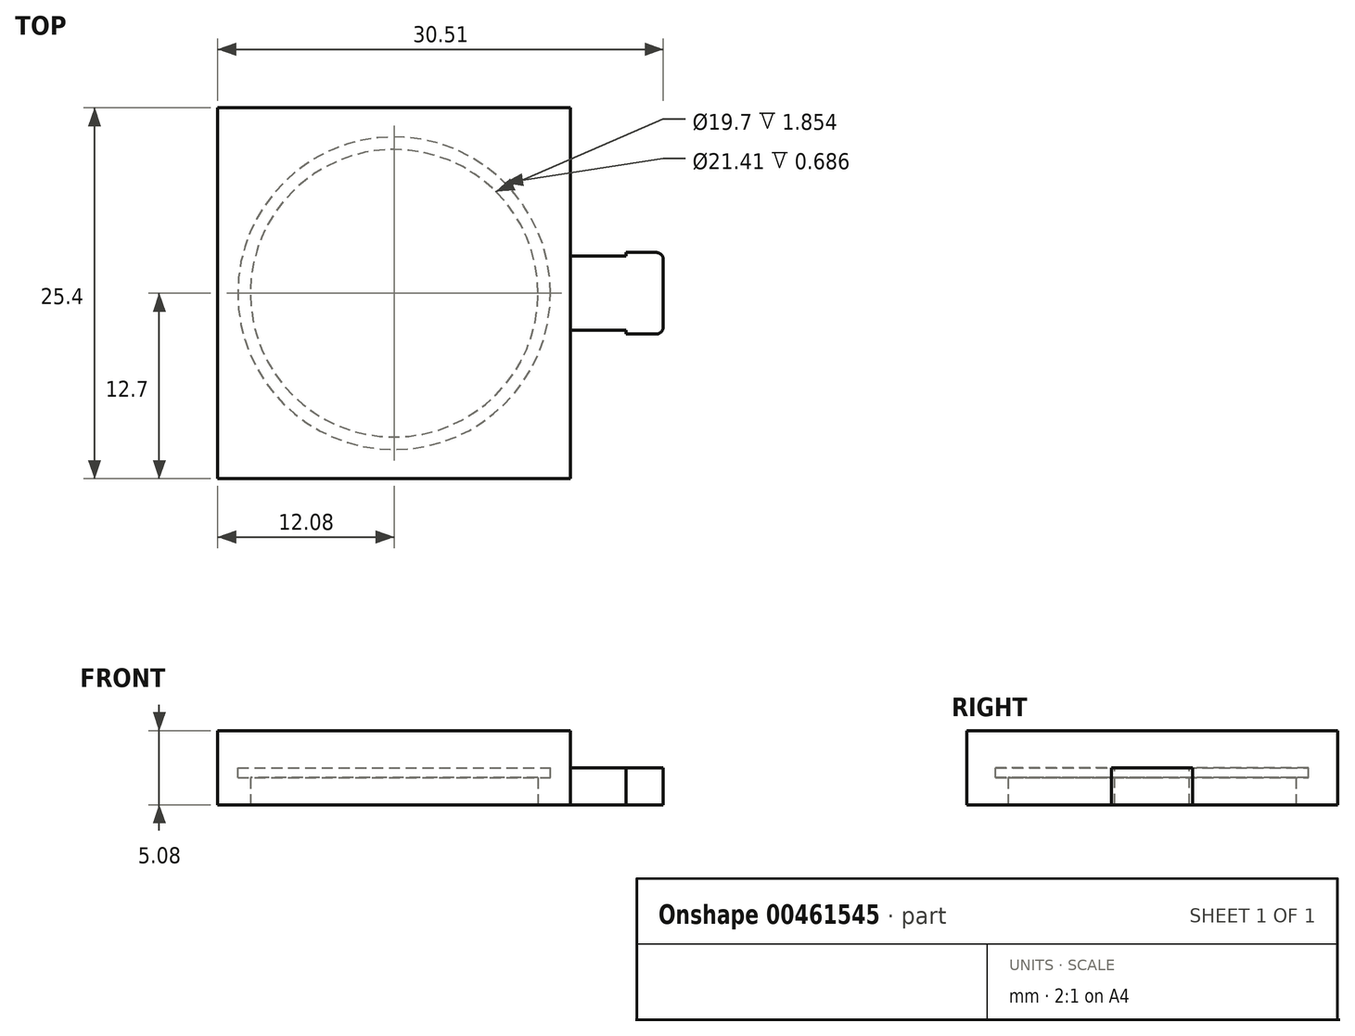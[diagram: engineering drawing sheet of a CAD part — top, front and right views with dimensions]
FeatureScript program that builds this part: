
annotation { "Feature Type Name" : "Feature", "Feature Type Description" : "" }
export const myFeature = defineFeature(function(context is Context, id is Id, definition is map)
    precondition{}
    {
        {
            var Q0;
            Q0=qCreatedBy(makeId("Top.planeOp"),FACE);
            var sketch = newSketch(context, id + "F0", { "sketchPlane" : qUnion([Q0])});
            skLineSegment(sketch, "E0.bottom", {"start": v(12.08, -12.7) * mm, "end": v(-12.08, -12.7) * mm});
            skLineSegment(sketch, "E0.top", {"start": v(12.08, 12.7) * mm, "end": v(-12.08, 12.7) * mm});
            skLineSegment(sketch, "E0.left", {"start": v(12.08, -12.7) * mm, "end": v(12.08, 12.7) * mm});
            skLineSegment(sketch, "E0.right", {"start": v(-12.08, -12.7) * mm, "end": v(-12.08, 12.7) * mm});
            skPoint(sketch, "E0.middle", {"position": v(0, 0) * mm});
            skSolve(sketch);
        }
        {
            var Q0;
            Q0 = qSketchRegion(id + "F0", true);
            extrude(context, id + "F1", {"entities" : qUnion([Q0]), "depth" : 5.08 * mm});
        }
        {
            var Q0;
            Q0=qCreatedBy(makeId("Top.planeOp"),FACE);
            var sketch = newSketch(context, id + "F2", { "sketchPlane" : qUnion([Q0])});
            skCircle(sketch, "E1", {"center": v(0, 0) * mm, "radius": 9.85 * mm});
            skSolve(sketch);
        }
        {
            var Q0;
            Q0=makeQuery(id+"F2.imprint","IMPRINT",FACE,{"disambiguationData":[TD([[makeQuery(id+"F2.imprint","IMPRINT",EDGE,{"derivedFrom":sQuery(id+"F2.wireOp",EDGE,"E1")}),1.0]])]});
            extrude(context, id + "F3", {"entities" : qUnion([Q0]), "operationType" : NewBodyOperationType.REMOVE, "depth" : 2.54 * mm});
        }
        {
            var Q0;
            Q0=makeQuery(id+"F3.boolean.opBoolean","COPY",FACE,{"derivedFrom":makeQuery(id+"F3.opExtrude","CAP_FACE",FACE,{"disambiguationData":[OSD([sQuery(id+"F2.wireOp",EDGE,"E1")])],"isStart":false})});
            var sketch = newSketch(context, id + "F4", { "sketchPlane" : qUnion([Q0])});
            skCircle(sketch, "E2", {"center": v(0, 0) * mm, "radius": 10.7 * mm});
            skSolve(sketch);
        }
        {
            var Q0;
            Q0=makeQuery(id+"F4.imprint","IMPRINT",FACE,{"disambiguationData":[TD([[makeQuery(id+"F4.imprint","IMPRINT",EDGE,{"derivedFrom":sQuery(id+"F4.wireOp",EDGE,"E2")}),1.0]])]});
            extrude(context, id + "F5", {"entities" : qUnion([Q0]), "operationType" : NewBodyOperationType.REMOVE, "depth" : 0.69 * mm});
        }
        {
            var Q0;
            Q0=makeQuery(id+"F1.opExtrude","SWEPT_FACE",FACE,{"disambiguationData":[OSD([sQuery(id+"F0.wireOp",EDGE,"E0.left")])]});
            var sketch = newSketch(context, id + "F6", { "sketchPlane" : qUnion([Q0])});
            skLineSegment(sketch, "E3.bottom", {"start": v(2.54, -2.54) * mm, "end": v(-2.54, -2.54) * mm});
            skLineSegment(sketch, "E3.top", {"start": v(2.54, 2.54) * mm, "end": v(-2.54, 2.54) * mm});
            skLineSegment(sketch, "E3.left", {"start": v(2.54, -2.54) * mm, "end": v(2.54, 2.54) * mm});
            skLineSegment(sketch, "E3.right", {"start": v(-2.54, -2.54) * mm, "end": v(-2.54, 2.54) * mm});
            skPoint(sketch, "E3.middle", {"position": v(0, 0) * mm});
            skSolve(sketch);
        }
        {
            var Q0;
            {var subQ0=sQuery(id+"F6.wireOp",EDGE,"E3.top");Q0=makeQuery(id+"F6.imprint","IMPRINT",FACE,{"disambiguationData":[TD([[makeQuery(id+"F6.imprint","IMPRINT",EDGE,{"derivedFrom":subQ0}),1.0]])]});}
            extrude(context, id + "F7", {"entities" : qUnion([Q0]), "operationType" : NewBodyOperationType.ADD, "depth" : 6.35 * mm});
        }
        {
            var Q0;
            Q0=makeQuery(id+"F7.opExtrude","SWEPT_FACE",FACE,{"disambiguationData":[OSD([sQuery(id+"F6.wireOp",EDGE,"E3.right")])]});
            var sketch = newSketch(context, id + "F8", { "sketchPlane" : qUnion([Q0])});
            skLineSegment(sketch, "E4.bottom", {"start": v(18.43, 2.54) * mm, "end": v(15.9, 2.54) * mm});
            skLineSegment(sketch, "E4.top", {"start": v(18.43, 0) * mm, "end": v(15.9, 0) * mm});
            skLineSegment(sketch, "E4.left", {"start": v(18.43, 2.54) * mm, "end": v(18.43, 0) * mm});
            skLineSegment(sketch, "E4.right", {"start": v(15.9, 2.54) * mm, "end": v(15.9, 0) * mm});
            skSolve(sketch);
        }
        {
            var Q0;
            Q0 = qSketchRegion(id + "F8", true);
            var Q1;
            Q1=makeQuery(id+"F8.imprint","IMPRINT",FACE,{"disambiguationData":[TD([[makeQuery(id+"F8.imprint","IMPRINT",EDGE,{"derivedFrom":sQuery(id+"F8.wireOp",EDGE,"E4.bottom")}),1.0]])]});
            extrude(context, id + "F9", {"entities" : qUnion([Q0, Q1]), "operationType" : NewBodyOperationType.ADD, "depth" : 0.25 * mm});
        }
        {
            var Q0;
            Q0=makeQuery(id+"F9.opExtrude","CAP_EDGE",EDGE,{"disambiguationData":[OSD([sQuery(id+"F8.wireOp",EDGE,"E4.left")])],"isStart":false});
            fillet(context, id + "F10", {"entities" : qUnion([Q0]), "radius" : 0.5 * mm, "tangentPropagation" : true, "allowEdgeOverflow" : false});
        }
        {
            var Q0;
            Q0=makeQuery(id+"F7.opExtrude","SWEPT_FACE",FACE,{"disambiguationData":[OSD([sQuery(id+"F6.wireOp",EDGE,"E3.left")])]});
            var sketch = newSketch(context, id + "F11", { "sketchPlane" : qUnion([Q0])});
            skLineSegment(sketch, "E5.bottom", {"start": v(-18.43, 2.54) * mm, "end": v(-15.9, 2.54) * mm});
            skLineSegment(sketch, "E5.top", {"start": v(-18.43, 0) * mm, "end": v(-15.9, 0) * mm});
            skLineSegment(sketch, "E5.left", {"start": v(-18.43, 2.54) * mm, "end": v(-18.43, 0) * mm});
            skLineSegment(sketch, "E5.right", {"start": v(-15.9, 2.54) * mm, "end": v(-15.9, 0) * mm});
            skSolve(sketch);
        }
        {
            var Q0;
            Q0=makeQuery(id+"F11.imprint","IMPRINT",FACE,{"disambiguationData":[TD([[makeQuery(id+"F11.imprint","IMPRINT",EDGE,{"derivedFrom":sQuery(id+"F11.wireOp",EDGE,"E5.bottom")}),-1.0]])]});
            extrude(context, id + "F12", {"entities" : qUnion([Q0]), "operationType" : NewBodyOperationType.ADD, "depth" : 0.25 * mm});
        }
        {
            var Q0;
            Q0=makeQuery(id+"F12.opExtrude","CAP_EDGE",EDGE,{"disambiguationData":[OSD([sQuery(id+"F11.wireOp",EDGE,"E5.left")])],"isStart":false});
            fillet(context, id + "F13", {"entities" : qUnion([Q0]), "radius" : 0.5 * mm, "tangentPropagation" : true, "allowEdgeOverflow" : false});
        }
    });
